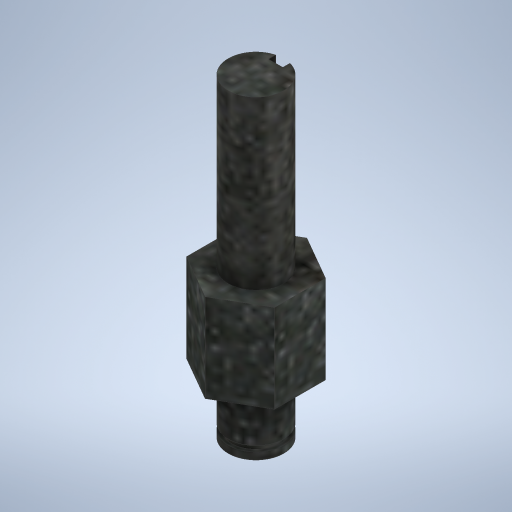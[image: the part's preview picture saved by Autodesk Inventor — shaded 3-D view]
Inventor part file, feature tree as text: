
AUTODESK INVENTOR PART (.ipt)
format: ipt  version: 2023 (Build 270158030, 158C)  size: 349,184 bytes
history: native  units: in
note: dims shown in document units (in); Inventor stores cm internally (conversion verified against a paired STEP export)
features: sketch x5, extrude x4, revolve x1
ambient origin geometry x8: Origin, YZ Plane, XZ Plane, XY Plane, X Axis, Y Axis, Z Axis, Center Point
bodies: Solid1 (feature_tree)
feature tree (10):
  extrude  "Extrusion1"  Depth=0.5in TaperAngle=0.0deg
  extrude  "Extrusion2"  Depth=1.0627in TaperAngle=0.0deg
  extrude  "Extrusion3"  Depth=0.081in
  revolve  "Revolution1"  [1 undecoded]
  extrude  "Extrusion4"  Depth=0.0394in
  sketch  "Sketch1"  dims[d0=0.5in d1=0.5in d2=0.0in]
  sketch  "Sketch2"  dims[d3=0.315in d4=1.0627in d5=0.0in]
  sketch  "Sketch3"  dims[d6=0.081in d8=0.046in]
  sketch  "Sketch4"  dims[d9=0.0in d10=0.0in d11=0.835in d12=0.0in]
  sketch  "Sketch5"  dims[d13=0.0315in d14=0.2756in d15=90.0deg d16=0.0394in d17=0.1155in d18=0.0in]
note: 1 required parameter value undecoded (feature->parameter linkage not recoverable at this tier; creation-order binding heuristic only, values carry confidence <= 0.55)
